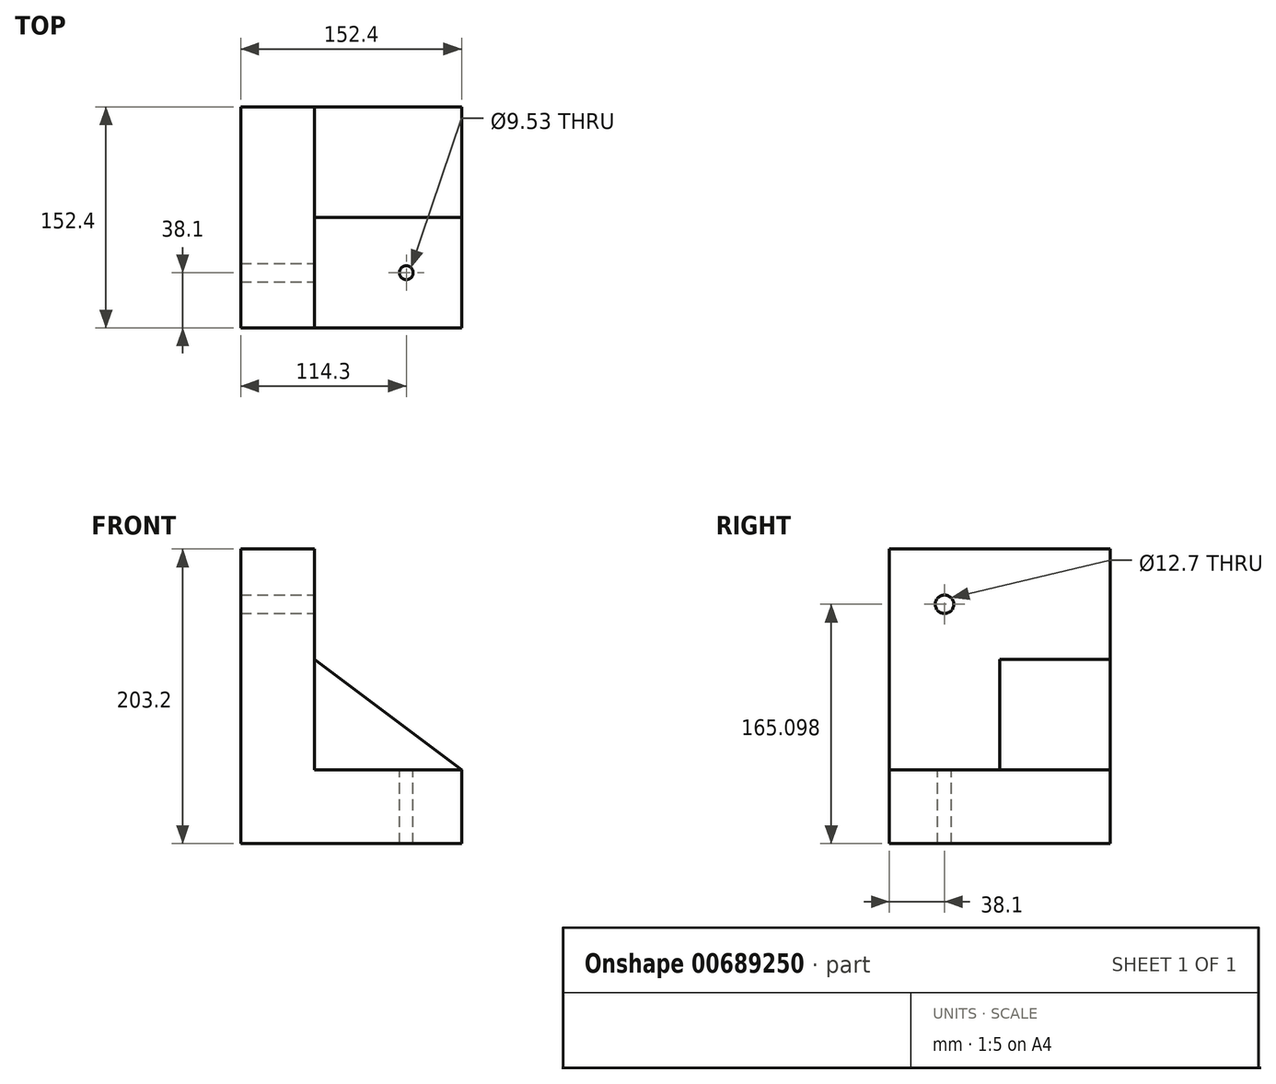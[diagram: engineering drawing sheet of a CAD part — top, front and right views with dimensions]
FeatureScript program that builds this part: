
annotation { "Feature Type Name" : "Feature", "Feature Type Description" : "" }
export const myFeature = defineFeature(function(context is Context, id is Id, definition is map)
    precondition{}
    {
        {
            var Q0;
            Q0=qCreatedBy(makeId("Front.planeOp"),FACE);
            var sketch = newSketch(context, id + "F0", { "sketchPlane" : qUnion([Q0])});
            skLineSegment(sketch, "E0", {"start": v(-50.8, 55.18) * mm, "end": v(-50.8, -148.02) * mm});
            skLineSegment(sketch, "E1", {"start": v(-50.8, -148.02) * mm, "end": v(101.6, -148.02) * mm});
            skLineSegment(sketch, "E2", {"start": v(101.6, -148.02) * mm, "end": v(101.6, -97.22) * mm});
            skLineSegment(sketch, "E3", {"start": v(101.6, -97.22) * mm, "end": v(0, -97.22) * mm});
            skLineSegment(sketch, "E4", {"start": v(0, -97.22) * mm, "end": v(0, 55.18) * mm});
            skLineSegment(sketch, "E5", {"start": v(-50.8, 55.18) * mm, "end": v(0, 55.18) * mm});
            skSolve(sketch);
        }
        {
            var Q0;
            Q0 = qSketchRegion(id + "F0", true);
            extrude(context, id + "F1", {"entities" : qUnion([Q0]), "depth" : 152.4 * mm, "offsetDistance" : 25.4 * mm});
        }
        {
            var Q0;
            Q0=makeQuery(id+"F1.opExtrude","SWEPT_FACE",FACE,{"disambiguationData":[OSD([sQuery(id+"F0.wireOp",EDGE,"E3")])]});
            var sketch = newSketch(context, id + "F2", { "sketchPlane" : qUnion([Q0])});
            skLineSegment(sketch, "E6.bottom", {"start": v(0, 0) * mm, "end": v(101.6, 0) * mm});
            skLineSegment(sketch, "E6.top", {"start": v(0, -76.2) * mm, "end": v(101.6, -76.2) * mm});
            skLineSegment(sketch, "E6.left", {"start": v(0, 0) * mm, "end": v(0, -76.2) * mm});
            skLineSegment(sketch, "E6.right", {"start": v(101.6, 0) * mm, "end": v(101.6, -76.2) * mm});
            skSolve(sketch);
        }
        {
            var Q0;
            Q0 = qSketchRegion(id + "F2", true);
            extrude(context, id + "F3", {"entities" : qUnion([Q0]), "operationType" : NewBodyOperationType.ADD, "depth" : 76.2 * mm, "offsetDistance" : 25.4 * mm});
        }
        {
            var Q0;
            Q0=makeQuery(id+"F3.opExtrude","SWEPT_FACE",FACE,{"disambiguationData":[OSD([sQuery(id+"F2.wireOp",EDGE,"E6.top")])]});
            var sketch = newSketch(context, id + "F4", { "sketchPlane" : qUnion([Q0])});
            skLineSegment(sketch, "E7", {"start": v(0, -21.02) * mm, "end": v(101.6, -97.22) * mm});
            skLineSegment(sketch, "E8", {"start": v(101.6, -97.22) * mm, "end": v(101.6, -21.02) * mm});
            skLineSegment(sketch, "E9", {"start": v(101.6, -21.02) * mm, "end": v(0, -21.02) * mm});
            skSolve(sketch);
        }
        {
            var Q0;
            Q0 = qSketchRegion(id + "F4", true);
            extrude(context, id + "F5", {"entities" : qUnion([Q0]), "operationType" : NewBodyOperationType.REMOVE, "oppositeDirection" : true, "depth" : 76.2 * mm, "offsetDistance" : 25.4 * mm});
        }
        {
            var Q0;
            Q0=makeQuery(id+"F1.opExtrude","SWEPT_FACE",FACE,{"disambiguationData":[OSD([sQuery(id+"F0.wireOp",EDGE,"E4")])]});
            var sketch = newSketch(context, id + "F6", { "sketchPlane" : qUnion([Q0])});
            skCircle(sketch, "E10", {"center": v(-114.3, 17.08) * mm, "radius": 4.76 * mm});
            skSolve(sketch);
        }
        {
            var Q0;
            Q0=makeQuery(id+"F1.opExtrude","SWEPT_FACE",FACE,{"disambiguationData":[OSD([sQuery(id+"F0.wireOp",EDGE,"E3")])]});
            var sketch = newSketch(context, id + "F7", { "sketchPlane" : qUnion([Q0])});
            skCircle(sketch, "E11", {"center": v(63.5, -114.3) * mm, "radius": 4.76 * mm});
            skSolve(sketch);
        }
        {
            var Q0;
            Q0=sQuery(id+"F7.wireOp",VERTEX,"E11.center");
            var Q1;
            Q1=makeQuery(id+"F1.opExtrude","SWEPT_BODY",BODY,{"disambiguationData":[OSD([sQuery(id+"F0.wireOp",EDGE,"E0"),sQuery(id+"F0.wireOp",EDGE,"E1"),sQuery(id+"F0.wireOp",EDGE,"E2"),sQuery(id+"F0.wireOp",EDGE,"E3"),sQuery(id+"F0.wireOp",EDGE,"E4"),sQuery(id+"F0.wireOp",EDGE,"E5")])]});
            hole(context, id + "F8", {"style" : HoleStyle.SIMPLE, "endStyle" : HoleEndStyle.THROUGH, "holeDiameter" : 9.52 * mm, "majorDiameter" : 6.35 * mm, "isTappedThrough" : true, "tappedDepth" : 12.7 * mm, "tapClearance" : 3, "locations" : qUnion([Q0]), "scope" : qUnion([Q1])});
        }
        {
            var Q0;
            Q0=sQuery(id+"F6.wireOp",VERTEX,"E10.center");
            var Q1;
            Q1=makeQuery(id+"F1.opExtrude","SWEPT_BODY",BODY,{"disambiguationData":[OSD([sQuery(id+"F0.wireOp",EDGE,"E0"),sQuery(id+"F0.wireOp",EDGE,"E1"),sQuery(id+"F0.wireOp",EDGE,"E2"),sQuery(id+"F0.wireOp",EDGE,"E3"),sQuery(id+"F0.wireOp",EDGE,"E4"),sQuery(id+"F0.wireOp",EDGE,"E5")])]});
            hole(context, id + "F9", {"style" : HoleStyle.SIMPLE, "endStyle" : HoleEndStyle.THROUGH, "holeDiameter" : 12.7 * mm, "majorDiameter" : 6.35 * mm, "isTappedThrough" : true, "tappedDepth" : 12.7 * mm, "tapClearance" : 3, "locations" : qUnion([Q0]), "scope" : qUnion([Q1])});
        }
    });
